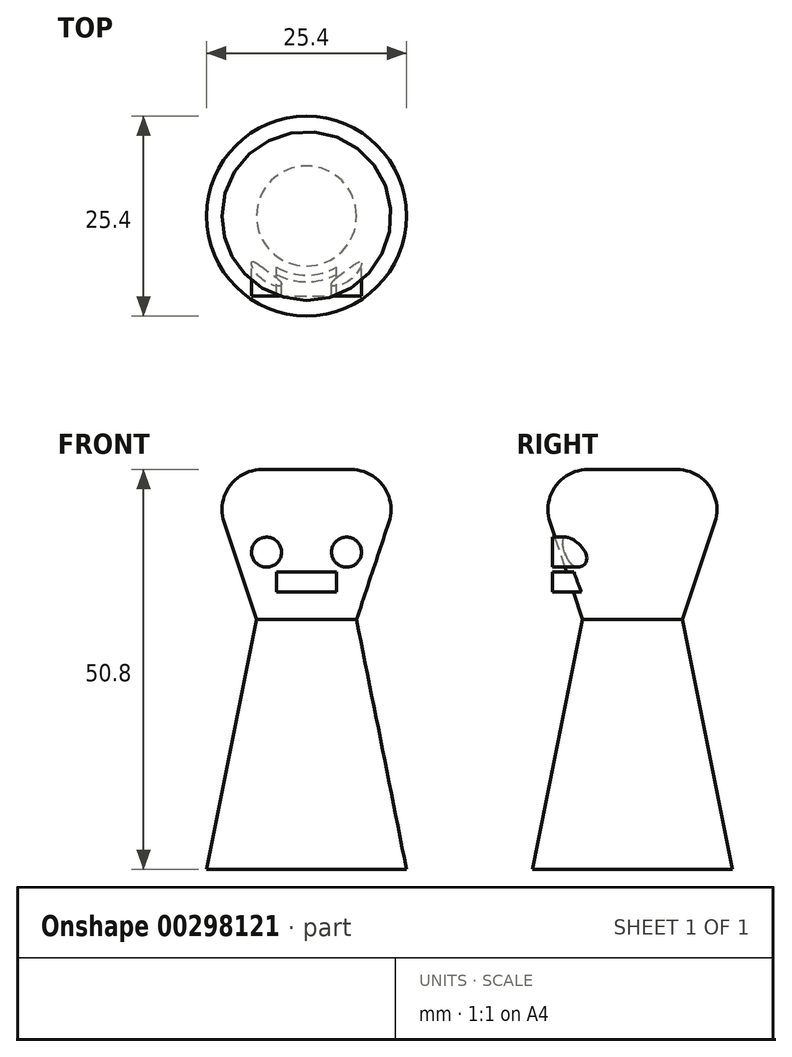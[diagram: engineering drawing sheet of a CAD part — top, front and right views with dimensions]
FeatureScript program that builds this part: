
annotation { "Feature Type Name" : "Feature", "Feature Type Description" : "" }
export const myFeature = defineFeature(function(context is Context, id is Id, definition is map)
    precondition{}
    {
        {
            var Q0;
            Q0=qCreatedBy(makeId("Front.planeOp"),FACE);
            var sketch = newSketch(context, id + "F0", { "sketchPlane" : qUnion([Q0])});
            skLineSegment(sketch, "E0", {"start": v(0, 0) * mm, "end": v(25.4, 0) * mm});
            skLineSegment(sketch, "E1", {"start": v(25.4, 0) * mm, "end": v(19.05, 31.75) * mm});
            skLineSegment(sketch, "E2", {"start": v(19.05, 31.75) * mm, "end": v(25.4, 50.8) * mm});
            skLineSegment(sketch, "E3", {"start": v(25.4, 50.8) * mm, "end": v(0, 50.8) * mm});
            skLineSegment(sketch, "E4", {"start": v(0, 50.8) * mm, "end": v(6.35, 31.75) * mm});
            skLineSegment(sketch, "E5", {"start": v(6.35, 31.75) * mm, "end": v(0, 0) * mm});
            skLineSegment(sketch, "E6", {"start": v(6.35, 31.75) * mm, "end": v(19.05, 31.75) * mm, "construction": true});
            skLineSegment(sketch, "E7", {"start": v(12.7, 50.8) * mm, "end": v(12.7, 0) * mm});
            skPoint(sketch, "E8", {"position": v(12.7, 31.75) * mm});
            skSolve(sketch);
        }
        {
            var Q0;
            {var subQ3=sQuery(id+"F0.wireOp",EDGE,"E1");Q0=makeQuery(id+"F0.imprint","IMPRINT",FACE,{"disambiguationData":[TD([[makeQuery(id+"F0.imprint","IMPRINT",EDGE,{"derivedFrom":subQ3}),1.0]])]});}
            var Q1;
            Q1=sQuery(id+"F0.wireOp",EDGE,"E7");
            revolve(context, id + "F1", {"entities" : qUnion([Q0]), "axis" : qUnion([Q1]), "revolveType" : RevolveType.FULL});
        }
        {
            var Q0;
            Q0=makeQuery(id+"F1.opRevolve","SWEPT_EDGE",EDGE,{"disambiguationData":[OSD([sQuery(id+"F0.wireOp",EDGE,"E2"),sQuery(id+"F0.wireOp",EDGE,"E3")])]});
            fillet(context, id + "F2", {"entities" : qUnion([Q0]), "radius" : 5.08 * mm, "tangentPropagation" : true, "allowEdgeOverflow" : false});
        }
        {
            var Q0;
            Q0=qCreatedBy(makeId("Front.planeOp"),FACE);
            var sketch = newSketch(context, id + "F3", { "sketchPlane" : qUnion([Q0])});
            skCircle(sketch, "E9", {"center": v(7.62, 40.3) * mm, "radius": 1.9 * mm});
            skCircle(sketch, "E10", {"center": v(17.78, 40.3) * mm, "radius": 1.9 * mm});
            skLineSegment(sketch, "E11.bottom", {"start": v(8.9, 37.76) * mm, "end": v(16.51, 37.76) * mm});
            skLineSegment(sketch, "E11.top", {"start": v(8.9, 35.22) * mm, "end": v(16.51, 35.22) * mm});
            skLineSegment(sketch, "E11.left", {"start": v(8.9, 37.76) * mm, "end": v(8.9, 35.22) * mm});
            skLineSegment(sketch, "E11.right", {"start": v(16.51, 37.76) * mm, "end": v(16.51, 35.22) * mm});
            skLineSegment(sketch, "E12", {"start": v(7.62, 40.3) * mm, "end": v(17.78, 40.3) * mm, "construction": true});
            skLineSegment(sketch, "E13", {"start": v(12.7, 40.3) * mm, "end": v(12.7, 44.11) * mm, "construction": true});
            skSolve(sketch);
        }
        {
            var Q0;
            Q0 = qSketchRegion(id + "F3", true);
            extrude(context, id + "F4", {"entities" : qUnion([Q0]), "operationType" : NewBodyOperationType.ADD, "depth" : 10.16 * mm});
        }
    });
